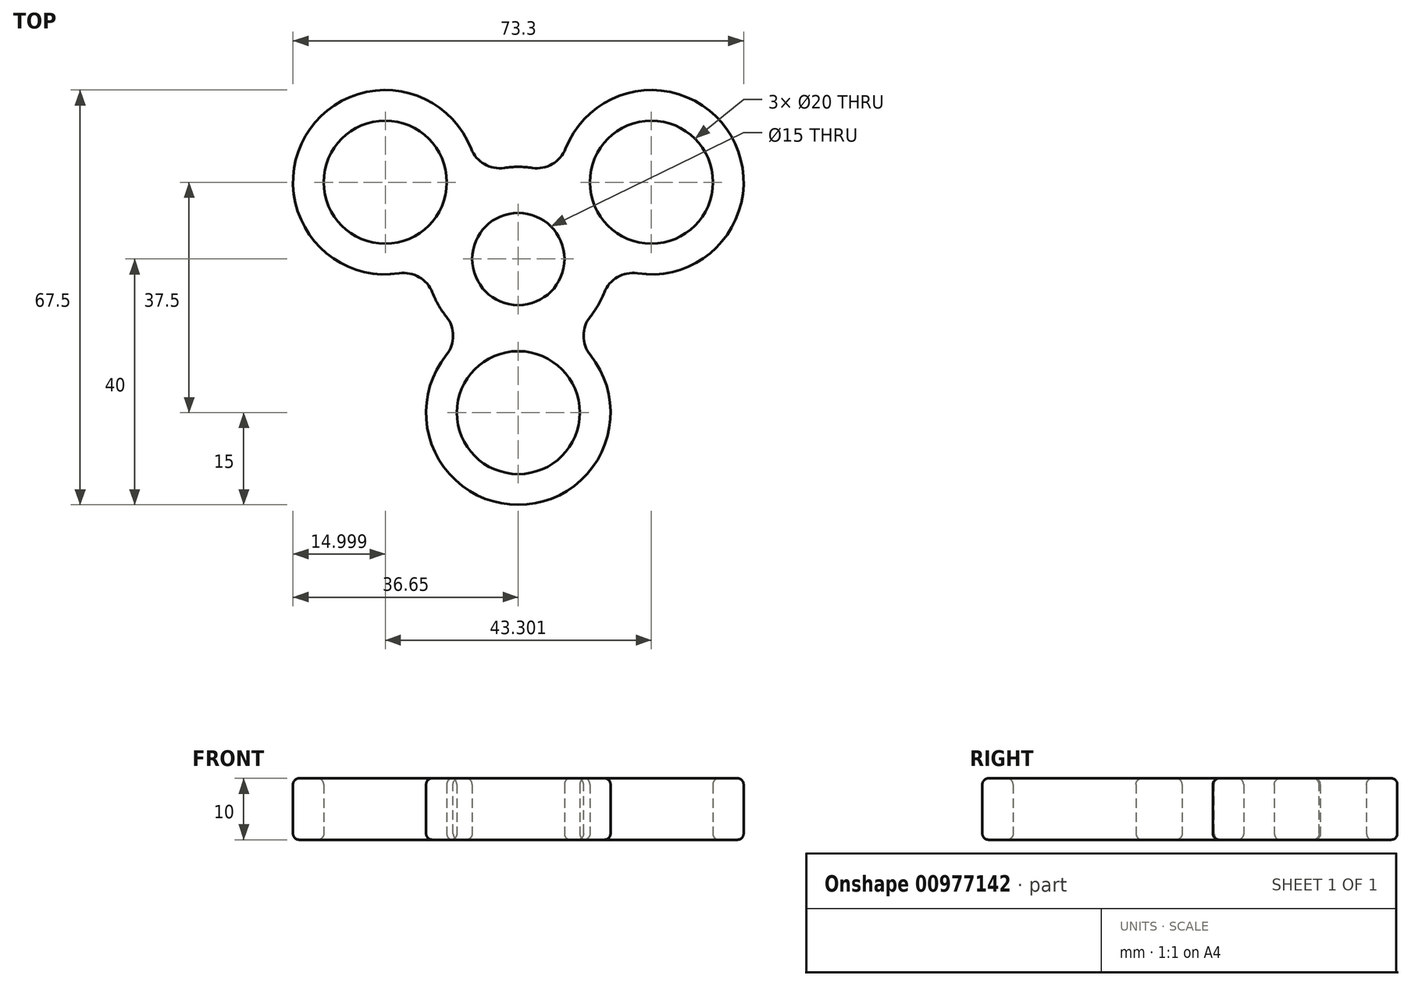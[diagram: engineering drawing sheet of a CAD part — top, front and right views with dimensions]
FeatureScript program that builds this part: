
annotation { "Feature Type Name" : "Feature", "Feature Type Description" : "" }
export const myFeature = defineFeature(function(context is Context, id is Id, definition is map)
    precondition{}
    {
        {
            var Q0;
            Q0=qCreatedBy(makeId("Top.planeOp"),FACE);
            var sketch = newSketch(context, id + "F0", { "sketchPlane" : qUnion([Q0])});
            skCircle(sketch, "E0", {"center": v(0, 0) * mm, "radius": 7.5 * mm});
            skCircle(sketch, "E1", {"center": v(0, 0) * mm, "radius": 15 * mm});
            skLineSegment(sketch, "E2", {"start": v(0, 0) * mm, "end": v(0, -25) * mm, "construction": true});
            skCircle(sketch, "E3", {"center": v(0, -25) * mm, "radius": 15 * mm});
            skCircle(sketch, "E4", {"center": v(0, -25) * mm, "radius": 10 * mm});
            skCircle(sketch, "E5.1.0", {"center": v(-21.65, 12.5) * mm, "radius": 15 * mm});
            skCircle(sketch, "E5.1.1", {"center": v(-21.65, 12.5) * mm, "radius": 10 * mm});
            skCircle(sketch, "E5.2.0", {"center": v(21.65, 12.5) * mm, "radius": 15 * mm});
            skCircle(sketch, "E5.2.1", {"center": v(21.65, 12.5) * mm, "radius": 10 * mm});
            skLineSegment(sketch, "E5.anchor2", {"start": v(0, 0) * mm, "end": v(21.65, 12.5) * mm, "construction": true});
            skSolve(sketch);
        }
        {
            var Q0;
            {var subQ3=sQuery(id+"F0.wireOp",EDGE,"E5.1.1");Q0=makeQuery(id+"F0.imprint","IMPRINT",FACE,{"disambiguationData":[TD([[makeQuery(id+"F0.imprint","IMPRINT",EDGE,{"derivedFrom":subQ3}),-1.0]])]});}
            var Q1;
            {var subQ0=sQuery(id+"F0.wireOp",EDGE,"E5.1.0");var subQ1=sQuery(id+"F0.wireOp",EDGE,"E1");var subQ2=makeQuery(id+"F0.imprint","INTERSECT",VERTEX,{"disambiguationData":[OD(0.0)],"derivedFrom":[subQ1,subQ0]});Q1=makeQuery(id+"F0.imprint","IMPRINT",FACE,{"disambiguationData":[TD([[makeQuery(id+"F0.imprint","IMPRINT",EDGE,{"disambiguationData":[TD([[subQ2,-1.0]])],"derivedFrom":subQ1}),1.0]])]});}
            var Q2;
            Q2=makeQuery(id+"F0.imprint","IMPRINT",FACE,{"disambiguationData":[TD([[makeQuery(id+"F0.imprint","IMPRINT",EDGE,{"derivedFrom":sQuery(id+"F0.wireOp",EDGE,"E0")}),-1.0]])]});
            var Q3;
            {var subQ0=sQuery(id+"F0.wireOp",EDGE,"E3");var subQ1=sQuery(id+"F0.wireOp",EDGE,"E1");var subQ2=makeQuery(id+"F0.imprint","INTERSECT",VERTEX,{"disambiguationData":[OD(0.0)],"derivedFrom":[subQ1,subQ0]});Q3=makeQuery(id+"F0.imprint","IMPRINT",FACE,{"disambiguationData":[TD([[makeQuery(id+"F0.imprint","IMPRINT",EDGE,{"disambiguationData":[TD([[subQ2,-1.0]])],"derivedFrom":subQ1}),1.0]])]});}
            var Q4;
            {var subQ3=sQuery(id+"F0.wireOp",EDGE,"E4");Q4=makeQuery(id+"F0.imprint","IMPRINT",FACE,{"disambiguationData":[TD([[makeQuery(id+"F0.imprint","IMPRINT",EDGE,{"derivedFrom":subQ3}),-1.0]])]});}
            var Q5;
            {var subQ0=sQuery(id+"F0.wireOp",EDGE,"E5.2.0");var subQ1=sQuery(id+"F0.wireOp",EDGE,"E1");var subQ2=makeQuery(id+"F0.imprint","INTERSECT",VERTEX,{"disambiguationData":[OD(0.0)],"derivedFrom":[subQ1,subQ0]});Q5=makeQuery(id+"F0.imprint","IMPRINT",FACE,{"disambiguationData":[TD([[makeQuery(id+"F0.imprint","IMPRINT",EDGE,{"disambiguationData":[TD([[subQ2,1.0]])],"derivedFrom":subQ1}),1.0]])]});}
            var Q6;
            {var subQ3=sQuery(id+"F0.wireOp",EDGE,"E5.2.1");Q6=makeQuery(id+"F0.imprint","IMPRINT",FACE,{"disambiguationData":[TD([[makeQuery(id+"F0.imprint","IMPRINT",EDGE,{"derivedFrom":subQ3}),-1.0]])]});}
            extrude(context, id + "F1", {"entities" : qUnion([Q0, Q1, Q2, Q3, Q4, Q5, Q6]), "depth" : 10 * mm, "offsetDistance" : 25 * mm});
        }
        {
            var Q0;
            {var subQ0=sQuery(id+"F0.wireOp",EDGE,"E5.2.0");var subQ1=sQuery(id+"F0.wireOp",EDGE,"E1");Q0=makeQuery(id+"F1.opExtrude","SWEPT_EDGE",EDGE,{"disambiguationData":[OSD([subQ1,subQ0]),TDD([makeQuery(id+"F0.imprint","INTERSECT",VERTEX,{"disambiguationData":[OD(1.0)],"derivedFrom":[subQ1,subQ0]})])]});}
            var Q1;
            {var subQ0=sQuery(id+"F0.wireOp",EDGE,"E3");var subQ1=sQuery(id+"F0.wireOp",EDGE,"E1");Q1=makeQuery(id+"F1.opExtrude","SWEPT_EDGE",EDGE,{"disambiguationData":[OSD([subQ1,subQ0]),TDD([makeQuery(id+"F0.imprint","INTERSECT",VERTEX,{"disambiguationData":[OD(1.0)],"derivedFrom":[subQ1,subQ0]})])]});}
            var Q2;
            {var subQ0=sQuery(id+"F0.wireOp",EDGE,"E3");var subQ1=sQuery(id+"F0.wireOp",EDGE,"E1");Q2=makeQuery(id+"F1.opExtrude","SWEPT_EDGE",EDGE,{"disambiguationData":[OSD([subQ1,subQ0]),TDD([makeQuery(id+"F0.imprint","INTERSECT",VERTEX,{"disambiguationData":[OD(0.0)],"derivedFrom":[subQ1,subQ0]})])]});}
            var Q3;
            {var subQ0=sQuery(id+"F0.wireOp",EDGE,"E5.1.0");var subQ1=sQuery(id+"F0.wireOp",EDGE,"E1");Q3=makeQuery(id+"F1.opExtrude","SWEPT_EDGE",EDGE,{"disambiguationData":[OSD([subQ1,subQ0]),TDD([makeQuery(id+"F0.imprint","INTERSECT",VERTEX,{"disambiguationData":[OD(1.0)],"derivedFrom":[subQ1,subQ0]})])]});}
            var Q4;
            {var subQ0=sQuery(id+"F0.wireOp",EDGE,"E5.1.0");var subQ1=sQuery(id+"F0.wireOp",EDGE,"E1");Q4=makeQuery(id+"F1.opExtrude","SWEPT_EDGE",EDGE,{"disambiguationData":[OSD([subQ1,subQ0]),TDD([makeQuery(id+"F0.imprint","INTERSECT",VERTEX,{"disambiguationData":[OD(0.0)],"derivedFrom":[subQ1,subQ0]})])]});}
            var Q5;
            {var subQ0=sQuery(id+"F0.wireOp",EDGE,"E5.2.0");var subQ1=sQuery(id+"F0.wireOp",EDGE,"E1");Q5=makeQuery(id+"F1.opExtrude","SWEPT_EDGE",EDGE,{"disambiguationData":[OSD([subQ1,subQ0]),TDD([makeQuery(id+"F0.imprint","INTERSECT",VERTEX,{"disambiguationData":[OD(0.0)],"derivedFrom":[subQ1,subQ0]})])]});}
            fillet(context, id + "F2", {"entities" : qUnion([Q0, Q1, Q2, Q3, Q4, Q5]), "radius" : 5 * mm, "tangentPropagation" : true, "allowEdgeOverflow" : false});
        }
        {
            var Q0;
            {var subQ0=sQuery(id+"F0.wireOp",EDGE,"E5.1.0");var subQ1=sQuery(id+"F0.wireOp",EDGE,"E1");Q0=makeQuery(id+"F2.opFillet","BLEND_EDGE",EDGE,{"blendedFrom":[makeQuery(id+"F1.opExtrude","SWEPT_EDGE",EDGE,{"disambiguationData":[OSD([subQ1,subQ0]),TDD([makeQuery(id+"F0.imprint","INTERSECT",VERTEX,{"disambiguationData":[OD(1.0)],"derivedFrom":[subQ1,subQ0]})])]}),makeQuery(id+"F1.opExtrude","CAP_FACE",FACE,{"disambiguationData":[OSD([sQuery(id+"F0.wireOp",EDGE,"E0"),subQ1,sQuery(id+"F0.wireOp",EDGE,"E3"),sQuery(id+"F0.wireOp",EDGE,"E4"),subQ0,sQuery(id+"F0.wireOp",EDGE,"E5.1.1"),sQuery(id+"F0.wireOp",EDGE,"E5.2.0"),sQuery(id+"F0.wireOp",EDGE,"E5.2.1")])],"isStart":true})],"blendedInto":[makeQuery(id+"F1.opExtrude","CAP_FACE",FACE,{"disambiguationData":[OSD([sQuery(id+"F0.wireOp",EDGE,"E0"),subQ1,sQuery(id+"F0.wireOp",EDGE,"E3"),sQuery(id+"F0.wireOp",EDGE,"E4"),subQ0,sQuery(id+"F0.wireOp",EDGE,"E5.1.1"),sQuery(id+"F0.wireOp",EDGE,"E5.2.0"),sQuery(id+"F0.wireOp",EDGE,"E5.2.1")])],"isStart":true})]});}
            var Q1;
            {var subQ0=sQuery(id+"F0.wireOp",EDGE,"E5.1.0");var subQ1=sQuery(id+"F0.wireOp",EDGE,"E1");Q1=makeQuery(id+"F2.opFillet","BLEND_EDGE",EDGE,{"blendedFrom":[makeQuery(id+"F1.opExtrude","SWEPT_EDGE",EDGE,{"disambiguationData":[OSD([subQ1,subQ0]),TDD([makeQuery(id+"F0.imprint","INTERSECT",VERTEX,{"disambiguationData":[OD(0.0)],"derivedFrom":[subQ1,subQ0]})])]}),makeQuery(id+"F1.opExtrude","CAP_FACE",FACE,{"disambiguationData":[OSD([sQuery(id+"F0.wireOp",EDGE,"E0"),subQ1,sQuery(id+"F0.wireOp",EDGE,"E3"),sQuery(id+"F0.wireOp",EDGE,"E4"),subQ0,sQuery(id+"F0.wireOp",EDGE,"E5.1.1"),sQuery(id+"F0.wireOp",EDGE,"E5.2.0"),sQuery(id+"F0.wireOp",EDGE,"E5.2.1")])],"isStart":true})],"blendedInto":[makeQuery(id+"F1.opExtrude","CAP_FACE",FACE,{"disambiguationData":[OSD([sQuery(id+"F0.wireOp",EDGE,"E0"),subQ1,sQuery(id+"F0.wireOp",EDGE,"E3"),sQuery(id+"F0.wireOp",EDGE,"E4"),subQ0,sQuery(id+"F0.wireOp",EDGE,"E5.1.1"),sQuery(id+"F0.wireOp",EDGE,"E5.2.0"),sQuery(id+"F0.wireOp",EDGE,"E5.2.1")])],"isStart":true})]});}
            var Q2;
            Q2=makeQuery(id+"F1.opExtrude","CAP_EDGE",EDGE,{"disambiguationData":[OSD([sQuery(id+"F0.wireOp",EDGE,"E0")])],"isStart":true});
            var Q3;
            Q3=makeQuery(id+"F1.opExtrude","CAP_EDGE",EDGE,{"disambiguationData":[OSD([sQuery(id+"F0.wireOp",EDGE,"E0")])],"isStart":false});
            var Q4;
            {var subQ0=sQuery(id+"F0.wireOp",EDGE,"E5.2.0");var subQ1=sQuery(id+"F0.wireOp",EDGE,"E1");Q4=makeQuery(id+"F2.opFillet","BLEND_EDGE",EDGE,{"blendedFrom":[makeQuery(id+"F1.opExtrude","SWEPT_EDGE",EDGE,{"disambiguationData":[OSD([subQ1,subQ0]),TDD([makeQuery(id+"F0.imprint","INTERSECT",VERTEX,{"disambiguationData":[OD(0.0)],"derivedFrom":[subQ1,subQ0]})])]}),makeQuery(id+"F1.opExtrude","CAP_FACE",FACE,{"disambiguationData":[OSD([sQuery(id+"F0.wireOp",EDGE,"E0"),subQ1,sQuery(id+"F0.wireOp",EDGE,"E3"),sQuery(id+"F0.wireOp",EDGE,"E4"),sQuery(id+"F0.wireOp",EDGE,"E5.1.0"),sQuery(id+"F0.wireOp",EDGE,"E5.1.1"),subQ0,sQuery(id+"F0.wireOp",EDGE,"E5.2.1")])],"isStart":false})],"blendedInto":[makeQuery(id+"F1.opExtrude","CAP_FACE",FACE,{"disambiguationData":[OSD([sQuery(id+"F0.wireOp",EDGE,"E0"),subQ1,sQuery(id+"F0.wireOp",EDGE,"E3"),sQuery(id+"F0.wireOp",EDGE,"E4"),sQuery(id+"F0.wireOp",EDGE,"E5.1.0"),sQuery(id+"F0.wireOp",EDGE,"E5.1.1"),subQ0,sQuery(id+"F0.wireOp",EDGE,"E5.2.1")])],"isStart":false})]});}
            var Q5;
            {var subQ0=sQuery(id+"F0.wireOp",EDGE,"E5.2.0");var subQ1=sQuery(id+"F0.wireOp",EDGE,"E1");Q5=makeQuery(id+"F2.opFillet","BLEND_EDGE",EDGE,{"blendedFrom":[makeQuery(id+"F1.opExtrude","SWEPT_EDGE",EDGE,{"disambiguationData":[OSD([subQ1,subQ0]),TDD([makeQuery(id+"F0.imprint","INTERSECT",VERTEX,{"disambiguationData":[OD(0.0)],"derivedFrom":[subQ1,subQ0]})])]}),makeQuery(id+"F1.opExtrude","CAP_FACE",FACE,{"disambiguationData":[OSD([sQuery(id+"F0.wireOp",EDGE,"E0"),subQ1,sQuery(id+"F0.wireOp",EDGE,"E3"),sQuery(id+"F0.wireOp",EDGE,"E4"),sQuery(id+"F0.wireOp",EDGE,"E5.1.0"),sQuery(id+"F0.wireOp",EDGE,"E5.1.1"),subQ0,sQuery(id+"F0.wireOp",EDGE,"E5.2.1")])],"isStart":true})],"blendedInto":[makeQuery(id+"F1.opExtrude","CAP_FACE",FACE,{"disambiguationData":[OSD([sQuery(id+"F0.wireOp",EDGE,"E0"),subQ1,sQuery(id+"F0.wireOp",EDGE,"E3"),sQuery(id+"F0.wireOp",EDGE,"E4"),sQuery(id+"F0.wireOp",EDGE,"E5.1.0"),sQuery(id+"F0.wireOp",EDGE,"E5.1.1"),subQ0,sQuery(id+"F0.wireOp",EDGE,"E5.2.1")])],"isStart":true})]});}
            var Q6;
            {var subQ0=sQuery(id+"F0.wireOp",EDGE,"E3");var subQ1=sQuery(id+"F0.wireOp",EDGE,"E1");Q6=makeQuery(id+"F2.opFillet","BLEND_EDGE",EDGE,{"blendedFrom":[makeQuery(id+"F1.opExtrude","SWEPT_EDGE",EDGE,{"disambiguationData":[OSD([subQ1,subQ0]),TDD([makeQuery(id+"F0.imprint","INTERSECT",VERTEX,{"disambiguationData":[OD(0.0)],"derivedFrom":[subQ1,subQ0]})])]}),makeQuery(id+"F1.opExtrude","CAP_FACE",FACE,{"disambiguationData":[OSD([sQuery(id+"F0.wireOp",EDGE,"E0"),subQ1,subQ0,sQuery(id+"F0.wireOp",EDGE,"E4"),sQuery(id+"F0.wireOp",EDGE,"E5.1.0"),sQuery(id+"F0.wireOp",EDGE,"E5.1.1"),sQuery(id+"F0.wireOp",EDGE,"E5.2.0"),sQuery(id+"F0.wireOp",EDGE,"E5.2.1")])],"isStart":false})],"blendedInto":[makeQuery(id+"F1.opExtrude","CAP_FACE",FACE,{"disambiguationData":[OSD([sQuery(id+"F0.wireOp",EDGE,"E0"),subQ1,subQ0,sQuery(id+"F0.wireOp",EDGE,"E4"),sQuery(id+"F0.wireOp",EDGE,"E5.1.0"),sQuery(id+"F0.wireOp",EDGE,"E5.1.1"),sQuery(id+"F0.wireOp",EDGE,"E5.2.0"),sQuery(id+"F0.wireOp",EDGE,"E5.2.1")])],"isStart":false})]});}
            var Q7;
            Q7=makeQuery(id+"F1.opExtrude","CAP_EDGE",EDGE,{"disambiguationData":[OSD([sQuery(id+"F0.wireOp",EDGE,"E4")])],"isStart":true});
            var Q8;
            Q8=makeQuery(id+"F1.opExtrude","CAP_EDGE",EDGE,{"disambiguationData":[OSD([sQuery(id+"F0.wireOp",EDGE,"E4")])],"isStart":false});
            var Q9;
            Q9=makeQuery(id+"F1.opExtrude","CAP_EDGE",EDGE,{"disambiguationData":[OSD([sQuery(id+"F0.wireOp",EDGE,"E5.1.1")])],"isStart":true});
            var Q10;
            Q10=makeQuery(id+"F1.opExtrude","CAP_EDGE",EDGE,{"disambiguationData":[OSD([sQuery(id+"F0.wireOp",EDGE,"E5.1.1")])],"isStart":false});
            var Q11;
            {var subQ0=sQuery(id+"F0.wireOp",EDGE,"E5.1.0");var subQ1=sQuery(id+"F0.wireOp",EDGE,"E1");Q11=makeQuery(id+"F2.opFillet","BLEND_EDGE",EDGE,{"blendedFrom":[makeQuery(id+"F1.opExtrude","SWEPT_EDGE",EDGE,{"disambiguationData":[OSD([subQ1,subQ0]),TDD([makeQuery(id+"F0.imprint","INTERSECT",VERTEX,{"disambiguationData":[OD(1.0)],"derivedFrom":[subQ1,subQ0]})])]}),makeQuery(id+"F1.opExtrude","CAP_FACE",FACE,{"disambiguationData":[OSD([sQuery(id+"F0.wireOp",EDGE,"E0"),subQ1,sQuery(id+"F0.wireOp",EDGE,"E3"),sQuery(id+"F0.wireOp",EDGE,"E4"),subQ0,sQuery(id+"F0.wireOp",EDGE,"E5.1.1"),sQuery(id+"F0.wireOp",EDGE,"E5.2.0"),sQuery(id+"F0.wireOp",EDGE,"E5.2.1")])],"isStart":false})],"blendedInto":[makeQuery(id+"F1.opExtrude","CAP_FACE",FACE,{"disambiguationData":[OSD([sQuery(id+"F0.wireOp",EDGE,"E0"),subQ1,sQuery(id+"F0.wireOp",EDGE,"E3"),sQuery(id+"F0.wireOp",EDGE,"E4"),subQ0,sQuery(id+"F0.wireOp",EDGE,"E5.1.1"),sQuery(id+"F0.wireOp",EDGE,"E5.2.0"),sQuery(id+"F0.wireOp",EDGE,"E5.2.1")])],"isStart":false})]});}
            var Q12;
            Q12=makeQuery(id+"F1.opExtrude","CAP_EDGE",EDGE,{"disambiguationData":[OSD([sQuery(id+"F0.wireOp",EDGE,"E5.2.1")])],"isStart":true});
            var Q13;
            Q13=makeQuery(id+"F1.opExtrude","CAP_EDGE",EDGE,{"disambiguationData":[OSD([sQuery(id+"F0.wireOp",EDGE,"E5.2.1")])],"isStart":false});
            var Q14;
            {var subQ0=sQuery(id+"F0.wireOp",EDGE,"E3");var subQ1=sQuery(id+"F0.wireOp",EDGE,"E1");Q14=makeQuery(id+"F2.opFillet","BLEND_EDGE",EDGE,{"blendedFrom":[makeQuery(id+"F1.opExtrude","SWEPT_EDGE",EDGE,{"disambiguationData":[OSD([subQ1,subQ0]),TDD([makeQuery(id+"F0.imprint","INTERSECT",VERTEX,{"disambiguationData":[OD(0.0)],"derivedFrom":[subQ1,subQ0]})])]}),makeQuery(id+"F1.opExtrude","CAP_FACE",FACE,{"disambiguationData":[OSD([sQuery(id+"F0.wireOp",EDGE,"E0"),subQ1,subQ0,sQuery(id+"F0.wireOp",EDGE,"E4"),sQuery(id+"F0.wireOp",EDGE,"E5.1.0"),sQuery(id+"F0.wireOp",EDGE,"E5.1.1"),sQuery(id+"F0.wireOp",EDGE,"E5.2.0"),sQuery(id+"F0.wireOp",EDGE,"E5.2.1")])],"isStart":true})],"blendedInto":[makeQuery(id+"F1.opExtrude","CAP_FACE",FACE,{"disambiguationData":[OSD([sQuery(id+"F0.wireOp",EDGE,"E0"),subQ1,subQ0,sQuery(id+"F0.wireOp",EDGE,"E4"),sQuery(id+"F0.wireOp",EDGE,"E5.1.0"),sQuery(id+"F0.wireOp",EDGE,"E5.1.1"),sQuery(id+"F0.wireOp",EDGE,"E5.2.0"),sQuery(id+"F0.wireOp",EDGE,"E5.2.1")])],"isStart":true})]});}
            var Q15;
            Q15=makeQuery(id+"F1.opExtrude","CAP_EDGE",EDGE,{"disambiguationData":[OSD([sQuery(id+"F0.wireOp",EDGE,"E3")])],"isStart":true});
            var Q16;
            Q16=makeQuery(id+"F1.opExtrude","CAP_EDGE",EDGE,{"disambiguationData":[OSD([sQuery(id+"F0.wireOp",EDGE,"E3")])],"isStart":false});
            var Q17;
            {var subQ0=sQuery(id+"F0.wireOp",EDGE,"E3");var subQ1=sQuery(id+"F0.wireOp",EDGE,"E1");Q17=makeQuery(id+"F2.opFillet","BLEND_EDGE",EDGE,{"blendedFrom":[makeQuery(id+"F1.opExtrude","SWEPT_EDGE",EDGE,{"disambiguationData":[OSD([subQ1,subQ0]),TDD([makeQuery(id+"F0.imprint","INTERSECT",VERTEX,{"disambiguationData":[OD(1.0)],"derivedFrom":[subQ1,subQ0]})])]}),makeQuery(id+"F1.opExtrude","CAP_FACE",FACE,{"disambiguationData":[OSD([sQuery(id+"F0.wireOp",EDGE,"E0"),subQ1,subQ0,sQuery(id+"F0.wireOp",EDGE,"E4"),sQuery(id+"F0.wireOp",EDGE,"E5.1.0"),sQuery(id+"F0.wireOp",EDGE,"E5.1.1"),sQuery(id+"F0.wireOp",EDGE,"E5.2.0"),sQuery(id+"F0.wireOp",EDGE,"E5.2.1")])],"isStart":true})],"blendedInto":[makeQuery(id+"F1.opExtrude","CAP_FACE",FACE,{"disambiguationData":[OSD([sQuery(id+"F0.wireOp",EDGE,"E0"),subQ1,subQ0,sQuery(id+"F0.wireOp",EDGE,"E4"),sQuery(id+"F0.wireOp",EDGE,"E5.1.0"),sQuery(id+"F0.wireOp",EDGE,"E5.1.1"),sQuery(id+"F0.wireOp",EDGE,"E5.2.0"),sQuery(id+"F0.wireOp",EDGE,"E5.2.1")])],"isStart":true})]});}
            var Q18;
            Q18=makeQuery(id+"F1.opExtrude","CAP_EDGE",EDGE,{"disambiguationData":[OSD([sQuery(id+"F0.wireOp",EDGE,"E5.1.0")])],"isStart":true});
            var Q19;
            Q19=makeQuery(id+"F1.opExtrude","CAP_EDGE",EDGE,{"disambiguationData":[OSD([sQuery(id+"F0.wireOp",EDGE,"E5.1.0")])],"isStart":false});
            var Q20;
            Q20=makeQuery(id+"F1.opExtrude","CAP_EDGE",EDGE,{"disambiguationData":[OSD([sQuery(id+"F0.wireOp",EDGE,"E5.2.0")])],"isStart":true});
            var Q21;
            Q21=makeQuery(id+"F1.opExtrude","CAP_EDGE",EDGE,{"disambiguationData":[OSD([sQuery(id+"F0.wireOp",EDGE,"E5.2.0")])],"isStart":false});
            var Q22;
            {var subQ0=sQuery(id+"F0.wireOp",EDGE,"E5.2.0");var subQ1=sQuery(id+"F0.wireOp",EDGE,"E1");Q22=makeQuery(id+"F2.opFillet","BLEND_EDGE",EDGE,{"blendedFrom":[makeQuery(id+"F1.opExtrude","SWEPT_EDGE",EDGE,{"disambiguationData":[OSD([subQ1,subQ0]),TDD([makeQuery(id+"F0.imprint","INTERSECT",VERTEX,{"disambiguationData":[OD(1.0)],"derivedFrom":[subQ1,subQ0]})])]}),makeQuery(id+"F1.opExtrude","CAP_FACE",FACE,{"disambiguationData":[OSD([sQuery(id+"F0.wireOp",EDGE,"E0"),subQ1,sQuery(id+"F0.wireOp",EDGE,"E3"),sQuery(id+"F0.wireOp",EDGE,"E4"),sQuery(id+"F0.wireOp",EDGE,"E5.1.0"),sQuery(id+"F0.wireOp",EDGE,"E5.1.1"),subQ0,sQuery(id+"F0.wireOp",EDGE,"E5.2.1")])],"isStart":true})],"blendedInto":[makeQuery(id+"F1.opExtrude","CAP_FACE",FACE,{"disambiguationData":[OSD([sQuery(id+"F0.wireOp",EDGE,"E0"),subQ1,sQuery(id+"F0.wireOp",EDGE,"E3"),sQuery(id+"F0.wireOp",EDGE,"E4"),sQuery(id+"F0.wireOp",EDGE,"E5.1.0"),sQuery(id+"F0.wireOp",EDGE,"E5.1.1"),subQ0,sQuery(id+"F0.wireOp",EDGE,"E5.2.1")])],"isStart":true})]});}
            var Q23;
            {var subQ0=sQuery(id+"F0.wireOp",EDGE,"E1");Q23=makeQuery(id+"F1.opExtrude","CAP_EDGE",EDGE,{"disambiguationData":[OSD([subQ0]),TDD([makeQuery(id+"F0.imprint","IMPRINT",EDGE,{"disambiguationData":[TD([[makeQuery(id+"F0.imprint","INTERSECT",VERTEX,{"disambiguationData":[OD(1.0)],"derivedFrom":[subQ0,sQuery(id+"F0.wireOp",EDGE,"E5.1.0")]}),-1.0]])],"derivedFrom":subQ0})])],"isStart":true});}
            var Q24;
            {var subQ0=sQuery(id+"F0.wireOp",EDGE,"E1");Q24=makeQuery(id+"F1.opExtrude","CAP_EDGE",EDGE,{"disambiguationData":[OSD([subQ0]),TDD([makeQuery(id+"F0.imprint","IMPRINT",EDGE,{"disambiguationData":[TD([[makeQuery(id+"F0.imprint","INTERSECT",VERTEX,{"disambiguationData":[OD(1.0)],"derivedFrom":[subQ0,sQuery(id+"F0.wireOp",EDGE,"E5.1.0")]}),-1.0]])],"derivedFrom":subQ0})])],"isStart":false});}
            var Q25;
            {var subQ0=sQuery(id+"F0.wireOp",EDGE,"E1");Q25=makeQuery(id+"F1.opExtrude","CAP_EDGE",EDGE,{"disambiguationData":[OSD([subQ0]),TDD([makeQuery(id+"F0.imprint","IMPRINT",EDGE,{"disambiguationData":[TD([[makeQuery(id+"F0.imprint","INTERSECT",VERTEX,{"disambiguationData":[OD(1.0)],"derivedFrom":[subQ0,sQuery(id+"F0.wireOp",EDGE,"E3")]}),-1.0]])],"derivedFrom":subQ0})])],"isStart":true});}
            var Q26;
            {var subQ0=sQuery(id+"F0.wireOp",EDGE,"E5.1.0");var subQ1=sQuery(id+"F0.wireOp",EDGE,"E1");Q26=makeQuery(id+"F2.opFillet","BLEND_EDGE",EDGE,{"blendedFrom":[makeQuery(id+"F1.opExtrude","SWEPT_EDGE",EDGE,{"disambiguationData":[OSD([subQ1,subQ0]),TDD([makeQuery(id+"F0.imprint","INTERSECT",VERTEX,{"disambiguationData":[OD(0.0)],"derivedFrom":[subQ1,subQ0]})])]}),makeQuery(id+"F1.opExtrude","SWEPT_FACE",FACE,{"disambiguationData":[OSD([subQ0])]})],"blendedInto":[makeQuery(id+"F1.opExtrude","SWEPT_FACE",FACE,{"disambiguationData":[OSD([subQ0])]})]});}
            var Q27;
            {var subQ0=sQuery(id+"F0.wireOp",EDGE,"E1");var subQ1=sQuery(id+"F0.wireOp",EDGE,"E5.1.0");var subQ2=makeQuery(id+"F0.imprint","INTERSECT",VERTEX,{"disambiguationData":[OD(0.0)],"derivedFrom":[subQ0,subQ1]});Q27=makeQuery(id+"F2.opFillet","BLEND_EDGE",EDGE,{"blendedFrom":[makeQuery(id+"F1.opExtrude","SWEPT_EDGE",EDGE,{"disambiguationData":[OSD([subQ0,subQ1]),TDD([subQ2])]}),makeQuery(id+"F1.opExtrude","SWEPT_FACE",FACE,{"disambiguationData":[OSD([subQ0]),TDD([makeQuery(id+"F0.imprint","IMPRINT",EDGE,{"disambiguationData":[TD([[makeQuery(id+"F0.imprint","INTERSECT",VERTEX,{"disambiguationData":[OD(0.0)],"derivedFrom":[subQ0,sQuery(id+"F0.wireOp",EDGE,"E5.2.0")]}),-1.0]])],"derivedFrom":subQ0})])]})],"blendedInto":[makeQuery(id+"F1.opExtrude","SWEPT_FACE",FACE,{"disambiguationData":[OSD([subQ0]),TDD([makeQuery(id+"F0.imprint","IMPRINT",EDGE,{"disambiguationData":[TD([[makeQuery(id+"F0.imprint","INTERSECT",VERTEX,{"disambiguationData":[OD(0.0)],"derivedFrom":[subQ0,sQuery(id+"F0.wireOp",EDGE,"E5.2.0")]}),-1.0]])],"derivedFrom":subQ0})])]})]});}
            var Q28;
            {var subQ0=sQuery(id+"F0.wireOp",EDGE,"E5.1.0");var subQ1=sQuery(id+"F0.wireOp",EDGE,"E1");Q28=makeQuery(id+"F2.opFillet","BLEND_EDGE",EDGE,{"blendedFrom":[makeQuery(id+"F1.opExtrude","SWEPT_EDGE",EDGE,{"disambiguationData":[OSD([subQ1,subQ0]),TDD([makeQuery(id+"F0.imprint","INTERSECT",VERTEX,{"disambiguationData":[OD(0.0)],"derivedFrom":[subQ1,subQ0]})])]}),makeQuery(id+"F1.opExtrude","CAP_FACE",FACE,{"disambiguationData":[OSD([sQuery(id+"F0.wireOp",EDGE,"E0"),subQ1,sQuery(id+"F0.wireOp",EDGE,"E3"),sQuery(id+"F0.wireOp",EDGE,"E4"),subQ0,sQuery(id+"F0.wireOp",EDGE,"E5.1.1"),sQuery(id+"F0.wireOp",EDGE,"E5.2.0"),sQuery(id+"F0.wireOp",EDGE,"E5.2.1")])],"isStart":false})],"blendedInto":[makeQuery(id+"F1.opExtrude","CAP_FACE",FACE,{"disambiguationData":[OSD([sQuery(id+"F0.wireOp",EDGE,"E0"),subQ1,sQuery(id+"F0.wireOp",EDGE,"E3"),sQuery(id+"F0.wireOp",EDGE,"E4"),subQ0,sQuery(id+"F0.wireOp",EDGE,"E5.1.1"),sQuery(id+"F0.wireOp",EDGE,"E5.2.0"),sQuery(id+"F0.wireOp",EDGE,"E5.2.1")])],"isStart":false})]});}
            var Q29;
            {var subQ0=sQuery(id+"F0.wireOp",EDGE,"E5.2.0");var subQ1=sQuery(id+"F0.wireOp",EDGE,"E1");Q29=makeQuery(id+"F2.opFillet","BLEND_EDGE",EDGE,{"blendedFrom":[makeQuery(id+"F1.opExtrude","SWEPT_EDGE",EDGE,{"disambiguationData":[OSD([subQ1,subQ0]),TDD([makeQuery(id+"F0.imprint","INTERSECT",VERTEX,{"disambiguationData":[OD(0.0)],"derivedFrom":[subQ1,subQ0]})])]}),makeQuery(id+"F1.opExtrude","SWEPT_FACE",FACE,{"disambiguationData":[OSD([subQ0])]})],"blendedInto":[makeQuery(id+"F1.opExtrude","SWEPT_FACE",FACE,{"disambiguationData":[OSD([subQ0])]})]});}
            var Q30;
            {var subQ0=sQuery(id+"F0.wireOp",EDGE,"E5.2.0");var subQ1=sQuery(id+"F0.wireOp",EDGE,"E1");var subQ2=makeQuery(id+"F0.imprint","INTERSECT",VERTEX,{"disambiguationData":[OD(0.0)],"derivedFrom":[subQ1,subQ0]});Q30=makeQuery(id+"F2.opFillet","BLEND_EDGE",EDGE,{"blendedFrom":[makeQuery(id+"F1.opExtrude","SWEPT_EDGE",EDGE,{"disambiguationData":[OSD([subQ1,subQ0]),TDD([subQ2])]}),makeQuery(id+"F1.opExtrude","SWEPT_FACE",FACE,{"disambiguationData":[OSD([subQ1]),TDD([makeQuery(id+"F0.imprint","IMPRINT",EDGE,{"disambiguationData":[TD([[subQ2,-1.0]])],"derivedFrom":subQ1})])]})],"blendedInto":[makeQuery(id+"F1.opExtrude","SWEPT_FACE",FACE,{"disambiguationData":[OSD([subQ1]),TDD([makeQuery(id+"F0.imprint","IMPRINT",EDGE,{"disambiguationData":[TD([[subQ2,-1.0]])],"derivedFrom":subQ1})])]})]});}
            var Q31;
            {var subQ0=sQuery(id+"F0.wireOp",EDGE,"E3");var subQ1=sQuery(id+"F0.wireOp",EDGE,"E1");Q31=makeQuery(id+"F2.opFillet","BLEND_EDGE",EDGE,{"blendedFrom":[makeQuery(id+"F1.opExtrude","SWEPT_EDGE",EDGE,{"disambiguationData":[OSD([subQ1,subQ0]),TDD([makeQuery(id+"F0.imprint","INTERSECT",VERTEX,{"disambiguationData":[OD(0.0)],"derivedFrom":[subQ1,subQ0]})])]}),makeQuery(id+"F1.opExtrude","SWEPT_FACE",FACE,{"disambiguationData":[OSD([subQ0])]})],"blendedInto":[makeQuery(id+"F1.opExtrude","SWEPT_FACE",FACE,{"disambiguationData":[OSD([subQ0])]})]});}
            var Q32;
            {var subQ0=sQuery(id+"F0.wireOp",EDGE,"E1");var subQ1=sQuery(id+"F0.wireOp",EDGE,"E3");var subQ2=makeQuery(id+"F0.imprint","INTERSECT",VERTEX,{"disambiguationData":[OD(0.0)],"derivedFrom":[subQ0,subQ1]});Q32=makeQuery(id+"F2.opFillet","BLEND_EDGE",EDGE,{"blendedFrom":[makeQuery(id+"F1.opExtrude","SWEPT_EDGE",EDGE,{"disambiguationData":[OSD([subQ0,subQ1]),TDD([subQ2])]}),makeQuery(id+"F1.opExtrude","SWEPT_FACE",FACE,{"disambiguationData":[OSD([subQ0]),TDD([makeQuery(id+"F0.imprint","IMPRINT",EDGE,{"disambiguationData":[TD([[makeQuery(id+"F0.imprint","INTERSECT",VERTEX,{"disambiguationData":[OD(1.0)],"derivedFrom":[subQ0,sQuery(id+"F0.wireOp",EDGE,"E5.1.0")]}),-1.0]])],"derivedFrom":subQ0})])]})],"blendedInto":[makeQuery(id+"F1.opExtrude","SWEPT_FACE",FACE,{"disambiguationData":[OSD([subQ0]),TDD([makeQuery(id+"F0.imprint","IMPRINT",EDGE,{"disambiguationData":[TD([[makeQuery(id+"F0.imprint","INTERSECT",VERTEX,{"disambiguationData":[OD(1.0)],"derivedFrom":[subQ0,sQuery(id+"F0.wireOp",EDGE,"E5.1.0")]}),-1.0]])],"derivedFrom":subQ0})])]})]});}
            var Q33;
            {var subQ0=sQuery(id+"F0.wireOp",EDGE,"E5.1.0");var subQ1=sQuery(id+"F0.wireOp",EDGE,"E1");var subQ2=makeQuery(id+"F0.imprint","INTERSECT",VERTEX,{"disambiguationData":[OD(1.0)],"derivedFrom":[subQ1,subQ0]});Q33=makeQuery(id+"F2.opFillet","BLEND_EDGE",EDGE,{"blendedFrom":[makeQuery(id+"F1.opExtrude","SWEPT_EDGE",EDGE,{"disambiguationData":[OSD([subQ1,subQ0]),TDD([subQ2])]}),makeQuery(id+"F1.opExtrude","SWEPT_FACE",FACE,{"disambiguationData":[OSD([subQ1]),TDD([makeQuery(id+"F0.imprint","IMPRINT",EDGE,{"disambiguationData":[TD([[subQ2,-1.0]])],"derivedFrom":subQ1})])]})],"blendedInto":[makeQuery(id+"F1.opExtrude","SWEPT_FACE",FACE,{"disambiguationData":[OSD([subQ1]),TDD([makeQuery(id+"F0.imprint","IMPRINT",EDGE,{"disambiguationData":[TD([[subQ2,-1.0]])],"derivedFrom":subQ1})])]})]});}
            var Q34;
            {var subQ0=sQuery(id+"F0.wireOp",EDGE,"E5.1.0");var subQ1=sQuery(id+"F0.wireOp",EDGE,"E1");Q34=makeQuery(id+"F2.opFillet","BLEND_EDGE",EDGE,{"blendedFrom":[makeQuery(id+"F1.opExtrude","SWEPT_EDGE",EDGE,{"disambiguationData":[OSD([subQ1,subQ0]),TDD([makeQuery(id+"F0.imprint","INTERSECT",VERTEX,{"disambiguationData":[OD(1.0)],"derivedFrom":[subQ1,subQ0]})])]}),makeQuery(id+"F1.opExtrude","SWEPT_FACE",FACE,{"disambiguationData":[OSD([subQ0])]})],"blendedInto":[makeQuery(id+"F1.opExtrude","SWEPT_FACE",FACE,{"disambiguationData":[OSD([subQ0])]})]});}
            var Q35;
            {var subQ0=sQuery(id+"F0.wireOp",EDGE,"E1");Q35=makeQuery(id+"F1.opExtrude","CAP_EDGE",EDGE,{"disambiguationData":[OSD([subQ0]),TDD([makeQuery(id+"F0.imprint","IMPRINT",EDGE,{"disambiguationData":[TD([[makeQuery(id+"F0.imprint","INTERSECT",VERTEX,{"disambiguationData":[OD(1.0)],"derivedFrom":[subQ0,sQuery(id+"F0.wireOp",EDGE,"E3")]}),-1.0]])],"derivedFrom":subQ0})])],"isStart":false});}
            var Q36;
            {var subQ0=sQuery(id+"F0.wireOp",EDGE,"E3");var subQ1=sQuery(id+"F0.wireOp",EDGE,"E1");Q36=makeQuery(id+"F2.opFillet","BLEND_EDGE",EDGE,{"blendedFrom":[makeQuery(id+"F1.opExtrude","SWEPT_EDGE",EDGE,{"disambiguationData":[OSD([subQ1,subQ0]),TDD([makeQuery(id+"F0.imprint","INTERSECT",VERTEX,{"disambiguationData":[OD(1.0)],"derivedFrom":[subQ1,subQ0]})])]}),makeQuery(id+"F1.opExtrude","CAP_FACE",FACE,{"disambiguationData":[OSD([sQuery(id+"F0.wireOp",EDGE,"E0"),subQ1,subQ0,sQuery(id+"F0.wireOp",EDGE,"E4"),sQuery(id+"F0.wireOp",EDGE,"E5.1.0"),sQuery(id+"F0.wireOp",EDGE,"E5.1.1"),sQuery(id+"F0.wireOp",EDGE,"E5.2.0"),sQuery(id+"F0.wireOp",EDGE,"E5.2.1")])],"isStart":false})],"blendedInto":[makeQuery(id+"F1.opExtrude","CAP_FACE",FACE,{"disambiguationData":[OSD([sQuery(id+"F0.wireOp",EDGE,"E0"),subQ1,subQ0,sQuery(id+"F0.wireOp",EDGE,"E4"),sQuery(id+"F0.wireOp",EDGE,"E5.1.0"),sQuery(id+"F0.wireOp",EDGE,"E5.1.1"),sQuery(id+"F0.wireOp",EDGE,"E5.2.0"),sQuery(id+"F0.wireOp",EDGE,"E5.2.1")])],"isStart":false})]});}
            var Q37;
            {var subQ0=sQuery(id+"F0.wireOp",EDGE,"E3");var subQ1=sQuery(id+"F0.wireOp",EDGE,"E1");var subQ2=makeQuery(id+"F0.imprint","INTERSECT",VERTEX,{"disambiguationData":[OD(1.0)],"derivedFrom":[subQ1,subQ0]});Q37=makeQuery(id+"F2.opFillet","BLEND_EDGE",EDGE,{"blendedFrom":[makeQuery(id+"F1.opExtrude","SWEPT_EDGE",EDGE,{"disambiguationData":[OSD([subQ1,subQ0]),TDD([subQ2])]}),makeQuery(id+"F1.opExtrude","SWEPT_FACE",FACE,{"disambiguationData":[OSD([subQ1]),TDD([makeQuery(id+"F0.imprint","IMPRINT",EDGE,{"disambiguationData":[TD([[subQ2,-1.0]])],"derivedFrom":subQ1})])]})],"blendedInto":[makeQuery(id+"F1.opExtrude","SWEPT_FACE",FACE,{"disambiguationData":[OSD([subQ1]),TDD([makeQuery(id+"F0.imprint","IMPRINT",EDGE,{"disambiguationData":[TD([[subQ2,-1.0]])],"derivedFrom":subQ1})])]})]});}
            var Q38;
            {var subQ0=sQuery(id+"F0.wireOp",EDGE,"E3");var subQ1=sQuery(id+"F0.wireOp",EDGE,"E1");Q38=makeQuery(id+"F2.opFillet","BLEND_EDGE",EDGE,{"blendedFrom":[makeQuery(id+"F1.opExtrude","SWEPT_EDGE",EDGE,{"disambiguationData":[OSD([subQ1,subQ0]),TDD([makeQuery(id+"F0.imprint","INTERSECT",VERTEX,{"disambiguationData":[OD(1.0)],"derivedFrom":[subQ1,subQ0]})])]}),makeQuery(id+"F1.opExtrude","SWEPT_FACE",FACE,{"disambiguationData":[OSD([subQ0])]})],"blendedInto":[makeQuery(id+"F1.opExtrude","SWEPT_FACE",FACE,{"disambiguationData":[OSD([subQ0])]})]});}
            var Q39;
            {var subQ0=sQuery(id+"F0.wireOp",EDGE,"E5.2.0");var subQ1=sQuery(id+"F0.wireOp",EDGE,"E1");Q39=makeQuery(id+"F2.opFillet","BLEND_EDGE",EDGE,{"blendedFrom":[makeQuery(id+"F1.opExtrude","SWEPT_EDGE",EDGE,{"disambiguationData":[OSD([subQ1,subQ0]),TDD([makeQuery(id+"F0.imprint","INTERSECT",VERTEX,{"disambiguationData":[OD(1.0)],"derivedFrom":[subQ1,subQ0]})])]}),makeQuery(id+"F1.opExtrude","CAP_FACE",FACE,{"disambiguationData":[OSD([sQuery(id+"F0.wireOp",EDGE,"E0"),subQ1,sQuery(id+"F0.wireOp",EDGE,"E3"),sQuery(id+"F0.wireOp",EDGE,"E4"),sQuery(id+"F0.wireOp",EDGE,"E5.1.0"),sQuery(id+"F0.wireOp",EDGE,"E5.1.1"),subQ0,sQuery(id+"F0.wireOp",EDGE,"E5.2.1")])],"isStart":false})],"blendedInto":[makeQuery(id+"F1.opExtrude","CAP_FACE",FACE,{"disambiguationData":[OSD([sQuery(id+"F0.wireOp",EDGE,"E0"),subQ1,sQuery(id+"F0.wireOp",EDGE,"E3"),sQuery(id+"F0.wireOp",EDGE,"E4"),sQuery(id+"F0.wireOp",EDGE,"E5.1.0"),sQuery(id+"F0.wireOp",EDGE,"E5.1.1"),subQ0,sQuery(id+"F0.wireOp",EDGE,"E5.2.1")])],"isStart":false})]});}
            var Q40;
            {var subQ0=sQuery(id+"F0.wireOp",EDGE,"E1");var subQ1=sQuery(id+"F0.wireOp",EDGE,"E5.2.0");var subQ2=makeQuery(id+"F0.imprint","INTERSECT",VERTEX,{"disambiguationData":[OD(1.0)],"derivedFrom":[subQ0,subQ1]});Q40=makeQuery(id+"F2.opFillet","BLEND_EDGE",EDGE,{"blendedFrom":[makeQuery(id+"F1.opExtrude","SWEPT_EDGE",EDGE,{"disambiguationData":[OSD([subQ0,subQ1]),TDD([subQ2])]}),makeQuery(id+"F1.opExtrude","SWEPT_FACE",FACE,{"disambiguationData":[OSD([subQ0]),TDD([makeQuery(id+"F0.imprint","IMPRINT",EDGE,{"disambiguationData":[TD([[makeQuery(id+"F0.imprint","INTERSECT",VERTEX,{"disambiguationData":[OD(1.0)],"derivedFrom":[subQ0,sQuery(id+"F0.wireOp",EDGE,"E3")]}),-1.0]])],"derivedFrom":subQ0})])]})],"blendedInto":[makeQuery(id+"F1.opExtrude","SWEPT_FACE",FACE,{"disambiguationData":[OSD([subQ0]),TDD([makeQuery(id+"F0.imprint","IMPRINT",EDGE,{"disambiguationData":[TD([[makeQuery(id+"F0.imprint","INTERSECT",VERTEX,{"disambiguationData":[OD(1.0)],"derivedFrom":[subQ0,sQuery(id+"F0.wireOp",EDGE,"E3")]}),-1.0]])],"derivedFrom":subQ0})])]})]});}
            var Q41;
            {var subQ0=sQuery(id+"F0.wireOp",EDGE,"E5.2.0");var subQ1=sQuery(id+"F0.wireOp",EDGE,"E1");Q41=makeQuery(id+"F2.opFillet","BLEND_EDGE",EDGE,{"blendedFrom":[makeQuery(id+"F1.opExtrude","SWEPT_EDGE",EDGE,{"disambiguationData":[OSD([subQ1,subQ0]),TDD([makeQuery(id+"F0.imprint","INTERSECT",VERTEX,{"disambiguationData":[OD(1.0)],"derivedFrom":[subQ1,subQ0]})])]}),makeQuery(id+"F1.opExtrude","SWEPT_FACE",FACE,{"disambiguationData":[OSD([subQ0])]})],"blendedInto":[makeQuery(id+"F1.opExtrude","SWEPT_FACE",FACE,{"disambiguationData":[OSD([subQ0])]})]});}
            var Q42;
            {var subQ0=sQuery(id+"F0.wireOp",EDGE,"E1");Q42=makeQuery(id+"F1.opExtrude","CAP_EDGE",EDGE,{"disambiguationData":[OSD([subQ0]),TDD([makeQuery(id+"F0.imprint","IMPRINT",EDGE,{"disambiguationData":[TD([[makeQuery(id+"F0.imprint","INTERSECT",VERTEX,{"disambiguationData":[OD(0.0)],"derivedFrom":[subQ0,sQuery(id+"F0.wireOp",EDGE,"E5.2.0")]}),-1.0]])],"derivedFrom":subQ0})])],"isStart":true});}
            var Q43;
            {var subQ0=sQuery(id+"F0.wireOp",EDGE,"E1");Q43=makeQuery(id+"F1.opExtrude","CAP_EDGE",EDGE,{"disambiguationData":[OSD([subQ0]),TDD([makeQuery(id+"F0.imprint","IMPRINT",EDGE,{"disambiguationData":[TD([[makeQuery(id+"F0.imprint","INTERSECT",VERTEX,{"disambiguationData":[OD(0.0)],"derivedFrom":[subQ0,sQuery(id+"F0.wireOp",EDGE,"E5.2.0")]}),-1.0]])],"derivedFrom":subQ0})])],"isStart":false});}
            fillet(context, id + "F3", {"entities" : qUnion([Q0, Q1, Q2, Q3, Q4, Q5, Q6, Q7, Q8, Q9, Q10, Q11, Q12, Q13, Q14, Q15, Q16, Q17, Q18, Q19, Q20, Q21, Q22, Q23, Q24, Q25, Q26, Q27, Q28, Q29, Q30, Q31, Q32, Q33, Q34, Q35, Q36, Q37, Q38, Q39, Q40, Q41, Q42, Q43]), "radius" : 1 * mm, "tangentPropagation" : true, "allowEdgeOverflow" : false});
        }
    });
